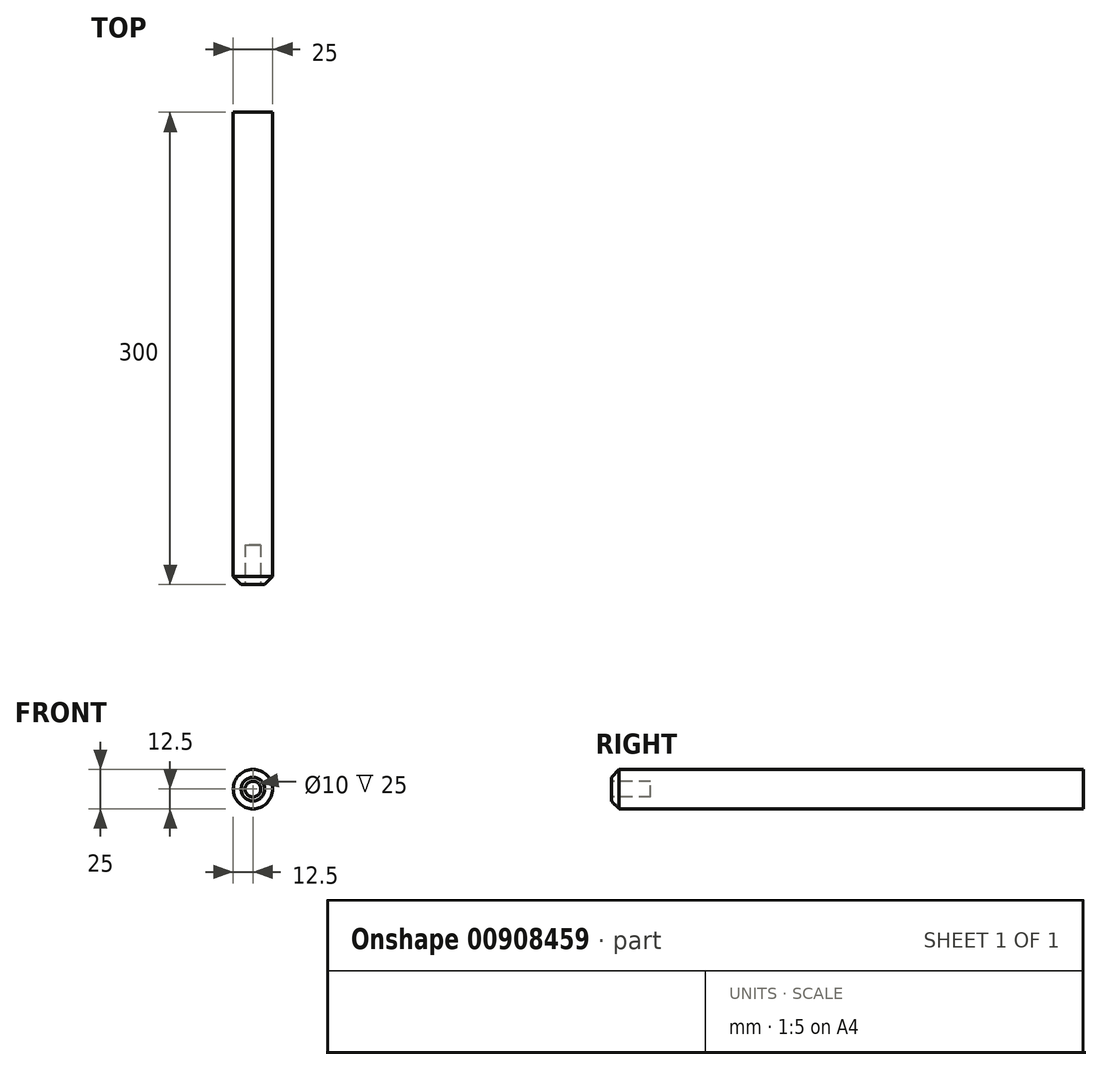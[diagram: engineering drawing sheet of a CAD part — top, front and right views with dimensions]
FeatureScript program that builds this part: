
annotation { "Feature Type Name" : "Feature", "Feature Type Description" : "" }
export const myFeature = defineFeature(function(context is Context, id is Id, definition is map)
    precondition{}
    {
        {
            var Q0;
            Q0=qCreatedBy(makeId("Front.planeOp"),FACE);
            var sketch = newSketch(context, id + "F0", { "sketchPlane" : qUnion([Q0])});
            skCircle(sketch, "E0", {"center": v(0, 0) * mm, "radius": 12.5 * mm});
            skSolve(sketch);
        }
        {
            var Q0;
            Q0 = qSketchRegion(id + "F0", true);
            extrude(context, id + "F1", {"entities" : qUnion([Q0]), "oppositeDirection" : true, "depth" : 300 * mm, "offsetDistance" : 25 * mm});
        }
        {
            var Q0;
            Q0=makeQuery(id+"F1.opExtrude","CAP_FACE",FACE,{"disambiguationData":[OSD([sQuery(id+"F0.wireOp",EDGE,"E0")])],"isStart":true});
            var sketch = newSketch(context, id + "F2", { "sketchPlane" : qUnion([Q0])});
            skCircle(sketch, "E1", {"center": v(0, 0) * mm, "radius": 5 * mm});
            skSolve(sketch);
        }
        {
            var Q0;
            Q0 = qSketchRegion(id + "F2", true);
            extrude(context, id + "F3", {"entities" : qUnion([Q0]), "operationType" : NewBodyOperationType.REMOVE, "oppositeDirection" : true, "depth" : 25 * mm, "offsetDistance" : 25 * mm});
        }
        {
            var Q0;
            Q0=makeQuery(id+"F1.opExtrude","CAP_EDGE",EDGE,{"disambiguationData":[OSD([sQuery(id+"F0.wireOp",EDGE,"E0")])],"isStart":true});
            chamfer(context, id + "F4", {"entities" : qUnion([Q0]), "width" : 5 * mm, "tangentPropagation" : true});
        }
    });
